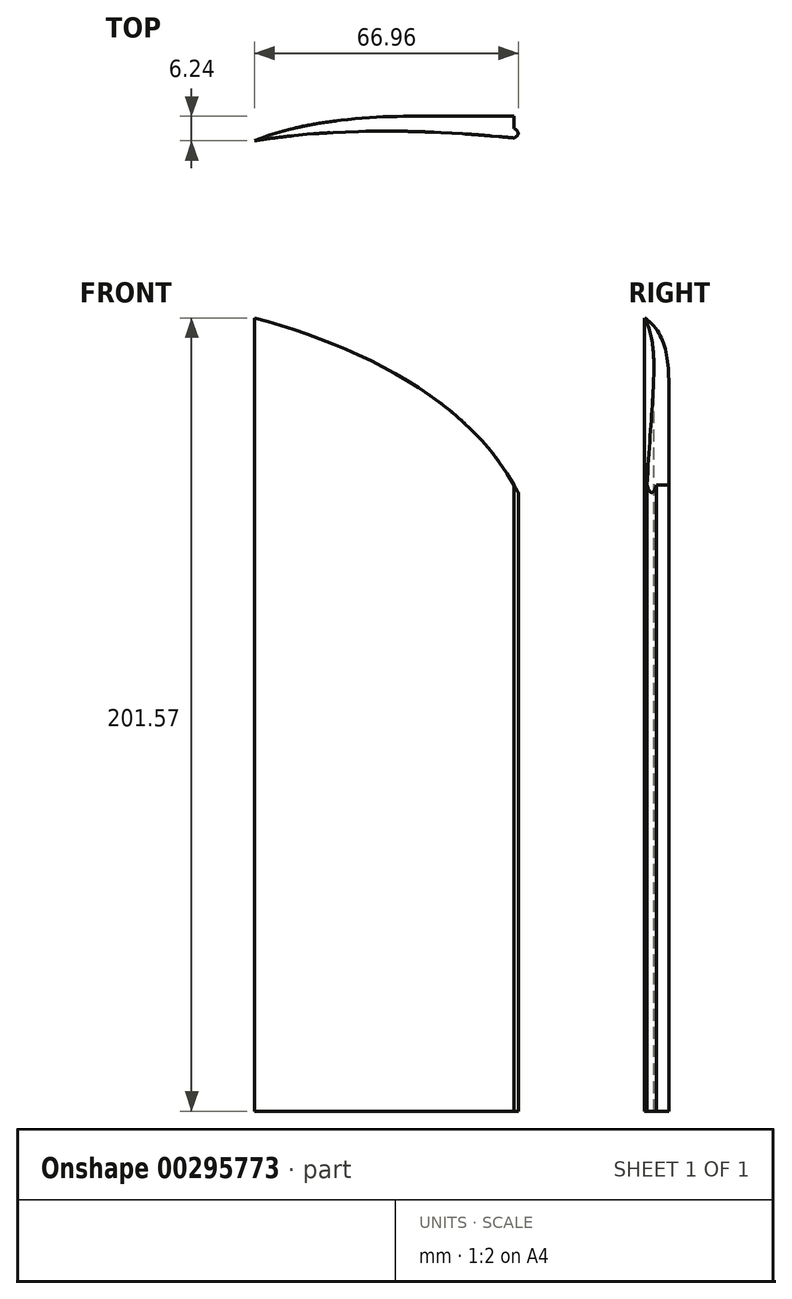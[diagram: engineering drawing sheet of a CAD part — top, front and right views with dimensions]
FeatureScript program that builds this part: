
annotation { "Feature Type Name" : "Feature", "Feature Type Description" : "" }
export const myFeature = defineFeature(function(context is Context, id is Id, definition is map)
    precondition{}
    {
        {
            var Q0;
            Q0=qCreatedBy(makeId("Top.planeOp"),FACE);
            var sketch = newSketch(context, id + "F0", { "sketchPlane" : qUnion([Q0])});
            skFitSpline(sketch, "E0", {"points": [v(-55.7, 43.35) * mm, v(10.23, 44.07) * mm], "startDerivative": vector(71.2, 30.93) * mm, "endDerivative": vector(-26.67, -15.49) * mm});
            skFitSpline(sketch, "E1", {"points": [v(-55.7, 43.35) * mm, v(10.23, 44.07) * mm], "startDerivative": vector(70.16, 11.25) * mm, "endDerivative": vector(57.65, -5.47) * mm});
            skLineSegment(sketch, "E2", {"start": v(-14.46, 49.6) * mm, "end": v(10.23, 49.6) * mm});
            skLineSegment(sketch, "E3", {"start": v(10.23, 49.6) * mm, "end": v(10.23, 44.07) * mm});
            skSolve(sketch);
        }
        {
            var Q0;
            Q0 = qSketchRegion(id + "F0", true);
            extrude(context, id + "F1", {"entities" : qUnion([Q0]), "depth" : 203.2 * mm});
        }
        {
            var Q0;
            Q0=qCreatedBy(makeId("Front.planeOp"),FACE);
            var sketch = newSketch(context, id + "F2", { "sketchPlane" : qUnion([Q0])});
            skFitSpline(sketch, "E4", {"points": [v(-86.53, 207.96) * mm, v(17.45, 136.29) * mm], "startDerivative": vector(184.93, -27.85) * mm, "endDerivative": vector(12.25, -115.86) * mm});
            skLineSegment(sketch, "E5", {"start": v(-86.53, 207.96) * mm, "end": v(61.64, 207.96) * mm});
            skLineSegment(sketch, "E6", {"start": v(61.64, 207.96) * mm, "end": v(17.45, 136.29) * mm});
            skSolve(sketch);
        }
        {
            var Q0;
            Q0 = qSketchRegion(id + "F2", true);
            extrude(context, id + "F3", {"entities" : qUnion([Q0]), "operationType" : NewBodyOperationType.REMOVE, "oppositeDirection" : true, "depth" : 156.2 * mm});
        }
    });
